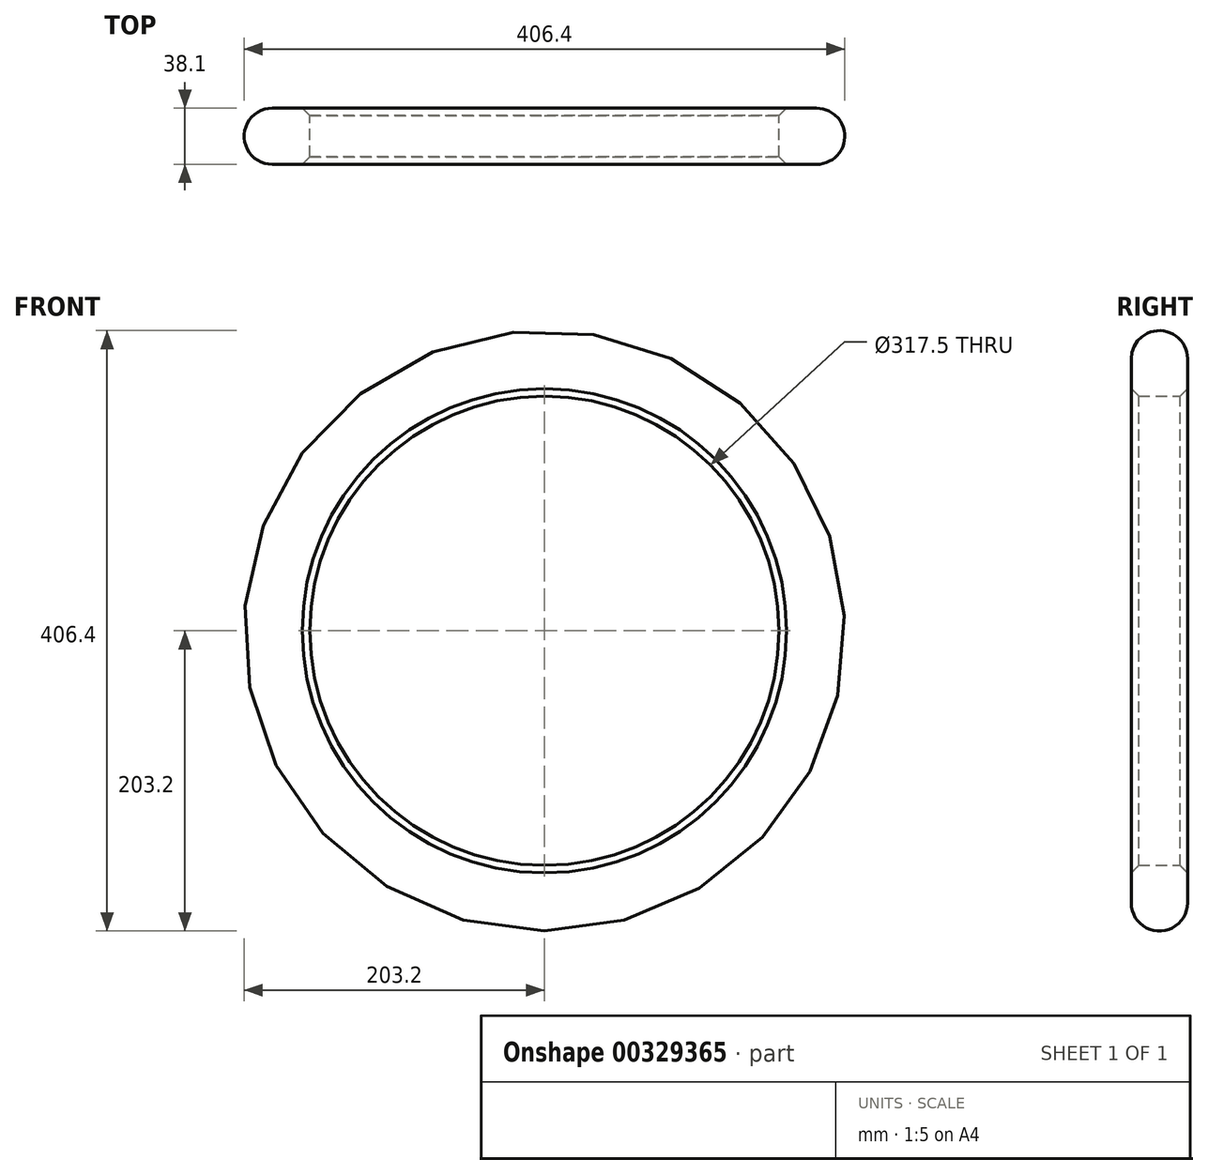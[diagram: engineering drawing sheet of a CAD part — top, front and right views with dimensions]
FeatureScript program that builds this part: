
annotation { "Feature Type Name" : "Feature", "Feature Type Description" : "" }
export const myFeature = defineFeature(function(context is Context, id is Id, definition is map)
    precondition{}
    {
        {
            var Q0;
            Q0=qCreatedBy(makeId("Front.planeOp"),FACE);
            var sketch = newSketch(context, id + "F0", { "sketchPlane" : qUnion([Q0])});
            skCircle(sketch, "E0", {"center": v(0, 0) * mm, "radius": 203.2 * mm});
            skCircle(sketch, "E1", {"center": v(0, 0) * mm, "radius": 158.75 * mm});
            skCircle(sketch, "E2", {"center": v(0, 0) * mm, "radius": 152.4 * mm});
            skCircle(sketch, "E3", {"center": v(0, 0) * mm, "radius": 25.4 * mm});
            skCircle(sketch, "E4", {"center": v(0, 0) * mm, "radius": 6.35 * mm});
            skSolve(sketch);
        }
        {
            var Q0;
            Q0=makeQuery(id+"F0.imprint","IMPRINT",FACE,{"disambiguationData":[TD([[makeQuery(id+"F0.imprint","IMPRINT",EDGE,{"derivedFrom":sQuery(id+"F0.wireOp",EDGE,"E0")}),1.0]])]});
            extrude(context, id + "F1", {"entities" : qUnion([Q0]), "depth" : 38.1 * mm});
        }
        {
            var Q0;
            Q0=makeQuery(id+"F1.opExtrude","CAP_EDGE",EDGE,{"disambiguationData":[OSD([sQuery(id+"F0.wireOp",EDGE,"E0")])],"isStart":false});
            var Q1;
            Q1=makeQuery(id+"F1.opExtrude","CAP_EDGE",EDGE,{"disambiguationData":[OSD([sQuery(id+"F0.wireOp",EDGE,"E0")])],"isStart":true});
            fillet(context, id + "F2", {"entities" : qUnion([Q0, Q1]), "radius" : 19.05 * mm, "tangentPropagation" : true, "allowEdgeOverflow" : false});
        }
        {
            var Q0;
            Q0=makeQuery(id+"F1.opExtrude","CAP_FACE",FACE,{"disambiguationData":[OSD([sQuery(id+"F0.wireOp",EDGE,"E0"),sQuery(id+"F0.wireOp",EDGE,"E1")])],"isStart":true});
            extrude(context, id + "F3", {"entities" : qUnion([Q0]), "operationType" : NewBodyOperationType.ADD, "oppositeDirection" : true, "depth" : 38.1 * mm});
        }
        {
            var Q0;
            Q0=makeQuery(id+"F1.opExtrude","CAP_EDGE",EDGE,{"disambiguationData":[OSD([sQuery(id+"F0.wireOp",EDGE,"E1")])],"isStart":false});
            chamfer(context, id + "F4", {"entities" : qUnion([Q0]), "width" : 5.08 * mm, "tangentPropagation" : true});
        }
        {
            var Q0;
            Q0=makeQuery(id+"F1.opExtrude","CAP_EDGE",EDGE,{"disambiguationData":[OSD([sQuery(id+"F0.wireOp",EDGE,"E1")])],"isStart":true});
            chamfer(context, id + "F5", {"entities" : qUnion([Q0]), "width" : 5.08 * mm, "tangentPropagation" : true});
        }
    });
